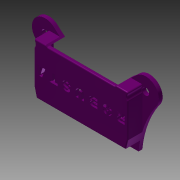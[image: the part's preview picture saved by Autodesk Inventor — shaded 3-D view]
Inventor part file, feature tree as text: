
AUTODESK INVENTOR PART (.ipt)
format: ipt  version: 2015 (Build 190159000, 159)  size: 722,944 bytes
history: native  units: mm
features: extrude x16, sketch x9, fillet x8, projected_geometry x5, plane x3, mirror x1
ambient origin geometry x8: Origin, YZ Plane, XZ Plane, XY Plane, X Axis, Y Axis, Z Axis, Center Point
bodies: Solid1 (feature_tree)
feature tree (42):
  extrude  "Extrusion1"  Depth=1.0mm
  extrude  "Extrusion2"  Depth=1.0mm
  extrude  "Extrusion3"  Depth=3.5mm TaperAngle=0.0deg
  extrude  "Extrusion4"  Depth=13.5mm TaperAngle=0.0deg
  extrude  "Extrusion6"  Depth=13.5mm TaperAngle=0.0deg
  extrude  "Extrusion7"  Depth=13.5mm TaperAngle=0.0deg
  extrude  "Extrusion8"  Depth=1.0mm
  plane  "Work Plane1"
  extrude  "Extrusion9"  Depth=1.0mm
  extrude  "Extrusion10"  [1 undecoded]
  extrude  "Extrusion11"  Depth=3.5mm TaperAngle=0.0deg
  fillet  "Fillet2"  Radius=3.5mm
  fillet  "Fillet4"  Radius=3.5mm
  fillet  "Fillet5"  Radius=1.0mm
  fillet  "Fillet6"  Radius=1.0mm
  plane  "Work Plane2"
  extrude  "Extrusion12"  Depth=1.0mm
  extrude  "Extrusion13"  Depth=1.0mm
  sketch  "Sketch18"  dims[d15=90.0deg d16=13.5mm d17=0.0mm]
  extrude  "Extrusion16"  TaperAngle=0.0deg  [1 undecoded]
  extrude  "Extrusion18"  Depth=1.0mm
  extrude  "Extrusion19"  TaperAngle=90.0deg  [1 undecoded]
  extrude  "Extrusion20"  TaperAngle=45.0deg  [1 undecoded]
  plane  "Work Plane3"
  mirror  "Mirror1"
  fillet  "Fillet7"  Radius=50.0mm
  fillet  "Fillet8"  Radius=3.178712mm
  fillet  "Fillet9"  Radius=50.0mm
  fillet  "Fillet10"  [1 undecoded]
  sketch  "Sketch7"  dims[d0=1.0mm d1=1.0mm]
  sketch  "Sketch10"  dims[d2=1.0mm d3=1.0mm]
  sketch  "Sketch11"  dims[d4=1.0mm d6=3.5mm d7=0.0mm]
  projected_geometry  "Projected Loop1"
  sketch  "Sketch12"  dims[d9=180.0deg d10=13.5mm d11=0.0mm]
  projected_geometry  "Projected Loop2"
  sketch  "Sketch15"  dims[d12=90.0deg d13=13.5mm d14=0.0mm]
  projected_geometry  "Projected Loop4"
  projected_geometry  "Projected Loop5"
  projected_geometry  "Projected Loop6"
  sketch  "Sketch19"  dims[d20=13.5mm d21=0.0mm d22=1.0mm]
  sketch  "Sketch20"  dims[d23=13.5mm d24=0.0mm d25=1.0mm]
  sketch  "Sketch23"  dims[d26=13.5mm d27=0.0mm d28=-13.5mm d29=3.5mm d30=0.0mm d31=3.5mm d32=0.0mm d33=3.5mm d34=0.0mm d38=1.0mm d40=1.0mm d41=1.0mm d42=1.0mm d43=0.0mm d44=4.125mm d45=90.0deg d46=45.0deg d47=50.0mm d48=0.0mm d49=3.178712mm d50=26.452487mm d51=50.0mm d52=0.0mm d61=90.0deg d64=1.0mm d65=1.0mm d68=1.0mm d69=1.0mm d73=3.5mm d74=0.0mm d83=0.25mm d84=0.25mm d85=0.25mm d86=3.5mm d87=0.0mm d90=0.75mm d91=3.5mm d92=0.0mm d98=6.5mm d99=6.5mm d100=10.0mm d101=0.0mm d102=0.0mm d103=1.0mm d104=1.0mm d105=1.0mm d106=1.0mm]
note: 5 required parameter values undecoded (feature->parameter linkage not recoverable at this tier; creation-order binding heuristic only, values carry confidence <= 0.55)
